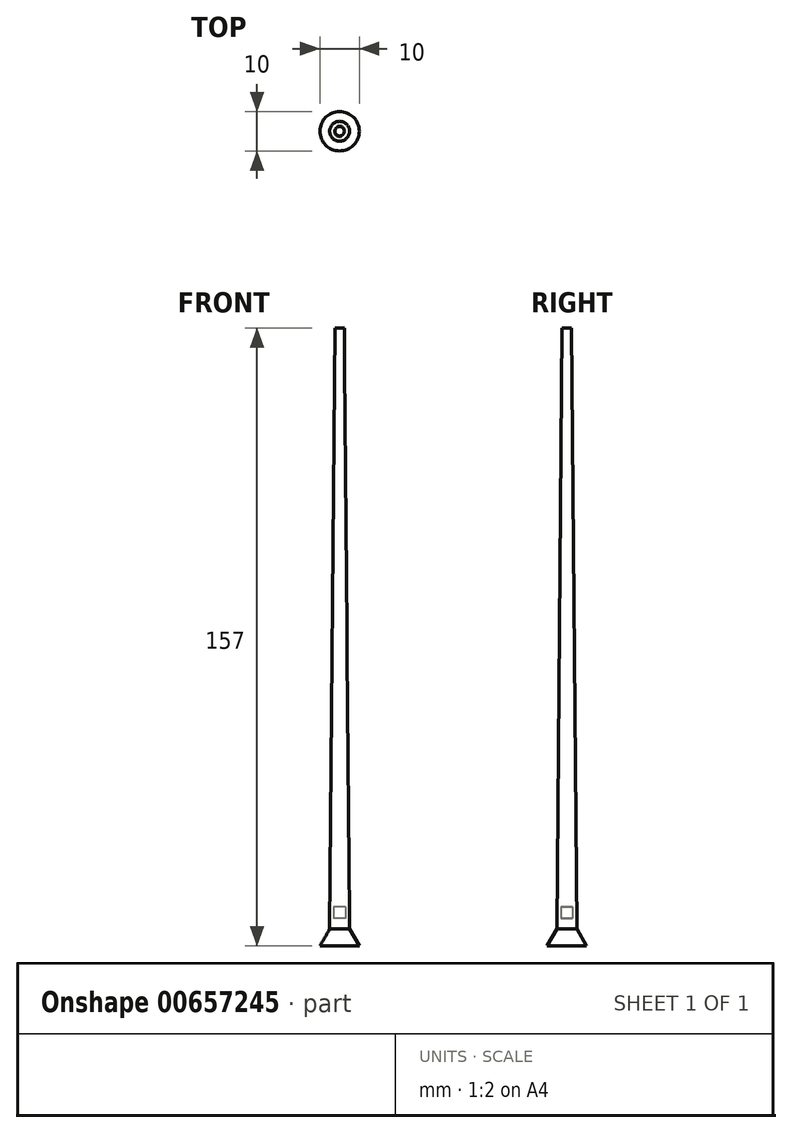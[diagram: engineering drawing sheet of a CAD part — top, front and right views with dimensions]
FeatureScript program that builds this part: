
annotation { "Feature Type Name" : "Feature", "Feature Type Description" : "" }
export const myFeature = defineFeature(function(context is Context, id is Id, definition is map)
    precondition{}
    {
        {
            var Q0;
            Q0=qCreatedBy(makeId("Top.planeOp"),FACE);
            var sketch = newSketch(context, id + "F0", { "sketchPlane" : qUnion([Q0])});
            skCircle(sketch, "E0", {"center": v(0, 0) * mm, "radius": 2.5 * mm});
            skSolve(sketch);
        }
        {
            var Q0;
            Q0=makeQuery(id+"F0.imprint","IMPRINT",FACE,{"disambiguationData":[TD([[makeQuery(id+"F0.imprint","IMPRINT",EDGE,{"derivedFrom":sQuery(id+"F0.wireOp",EDGE,"E0")}),1.0]])]});
            extrude(context, id + "F1", {"entities" : qUnion([Q0]), "depth" : 150 * mm, "offsetDistance" : 25 * mm, "hasDraft" : true, "draftAngle" : .5 * degree, "draftPullDirection" : true});
        }
        {
            var Q0;
            Q0=makeQuery(id+"F1.opExtrude","CAP_FACE",FACE,{"disambiguationData":[OSD([sQuery(id+"F0.wireOp",EDGE,"E0")])],"isStart":true});
            var sketch = newSketch(context, id + "F2", { "sketchPlane" : qUnion([Q0])});
            skCircle(sketch, "E1", {"center": v(0, 0) * mm, "radius": 5 * mm});
            skSolve(sketch);
        }
        {
            var Q0;
            Q0=makeQuery(id+"F2.imprint","IMPRINT",FACE,{"disambiguationData":[TD([[makeQuery(id+"F2.imprint","IMPRINT",EDGE,{"derivedFrom":sQuery(id+"F2.wireOp",EDGE,"E1")}),1.0]])]});
            var Q1;
            Q1=makeQuery(id+"F2.imprint","IMPRINT",FACE,{"disambiguationData":[TD([[makeQuery(id+"F2.imprint","IMPRINT",EDGE,{"derivedFrom":makeQuery(id+"F1.opExtrude","CAP_EDGE",EDGE,{"disambiguationData":[OSD([sQuery(id+"F0.wireOp",EDGE,"E0")])],"isStart":true})}),-1.0]])]});
            extrude(context, id + "F3", {"entities" : qUnion([Q0, Q1]), "operationType" : NewBodyOperationType.ADD, "depth" : 7 * mm, "offsetDistance" : 25 * mm});
        }
        {
            var Q0;
            Q0=makeQuery(id+"F3.opExtrude","CAP_EDGE",EDGE,{"disambiguationData":[OSD([sQuery(id+"F2.wireOp",EDGE,"E1")])],"isStart":true});
            chamfer(context, id + "F4", {"entities" : qUnion([Q0]), "chamferType" : ChamferType.OFFSET_ANGLE, "width" : 7 * mm, "oppositeDirection" : false, "angle" : 30 * degree, "tangentPropagation" : true});
        }
        {
            var Q0;
            Q0=qCreatedBy(makeId("Top.planeOp"),FACE);
            var sketch = newSketch(context, id + "F5", { "sketchPlane" : qUnion([Q0])});
            skCircle(sketch, "E2", {"center": v(0, 0) * mm, "radius": 1.5 * mm});
            skSolve(sketch);
        }
        {
            var Q0;
            Q0=makeQuery(id+"F5.imprint","IMPRINT",FACE,{"disambiguationData":[TD([[makeQuery(id+"F5.imprint","IMPRINT",EDGE,{"derivedFrom":sQuery(id+"F5.wireOp",EDGE,"E2")}),1.0]])]});
            extrude(context, id + "F6", {"entities" : qUnion([Q0]), "depth" : 3 * mm, "offsetDistance" : 25 * mm});
        }
    });
